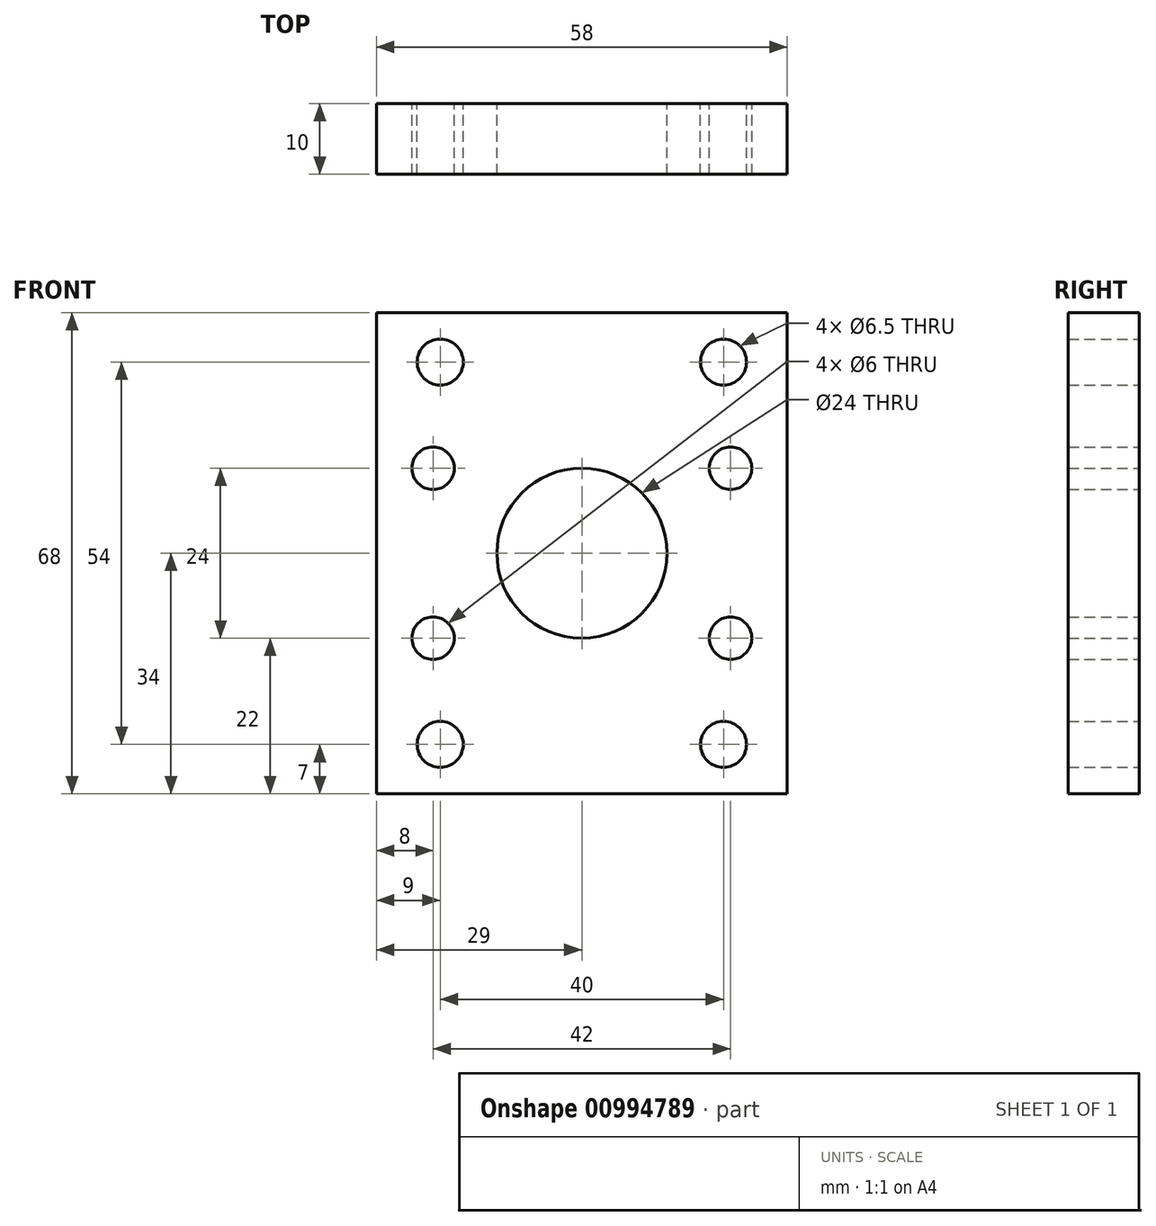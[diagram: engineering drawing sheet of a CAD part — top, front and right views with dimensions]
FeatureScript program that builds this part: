
annotation { "Feature Type Name" : "Feature", "Feature Type Description" : "" }
export const myFeature = defineFeature(function(context is Context, id is Id, definition is map)
    precondition{}
    {
        {
            var Q0;
            Q0=qCreatedBy(makeId("Front.planeOp"),FACE);
            var sketch = newSketch(context, id + "F0", { "sketchPlane" : qUnion([Q0])});
            skLineSegment(sketch, "E0.bottom", {"start": v(-29, 34) * mm, "end": v(29, 34) * mm});
            skLineSegment(sketch, "E0.top", {"start": v(-29, -34) * mm, "end": v(29, -34) * mm});
            skLineSegment(sketch, "E0.left", {"start": v(-29, 34) * mm, "end": v(-29, -34) * mm});
            skLineSegment(sketch, "E0.right", {"start": v(29, 34) * mm, "end": v(29, -34) * mm});
            skPoint(sketch, "E0.middle", {"position": v(0, 0) * mm});
            skCircle(sketch, "E1", {"center": v(0, 0) * mm, "radius": 12 * mm});
            skCircle(sketch, "E2", {"center": v(-20, -27) * mm, "radius": 3.25 * mm});
            skCircle(sketch, "E3", {"center": v(20, -27) * mm, "radius": 3.25 * mm});
            skCircle(sketch, "E4.MirrorC", {"center": v(-20, 27) * mm, "radius": 3.25 * mm});
            skCircle(sketch, "E5.MirrorC", {"center": v(20, 27) * mm, "radius": 3.25 * mm});
            skCircle(sketch, "E6", {"center": v(-21, 12) * mm, "radius": 3 * mm});
            skCircle(sketch, "E7.MirrorC", {"center": v(-21, -12) * mm, "radius": 3 * mm});
            skCircle(sketch, "E8.MirrorC", {"center": v(21, 12) * mm, "radius": 3 * mm});
            skCircle(sketch, "E9.MirrorC", {"center": v(21, -12) * mm, "radius": 3 * mm});
            skSolve(sketch);
        }
        {
            var Q0;
            Q0 = qSketchRegion(id + "F0", true);
            extrude(context, id + "F1", {"entities" : qUnion([Q0]), "depth" : 10 * mm, "offsetDistance" : 25 * mm});
        }
    });
